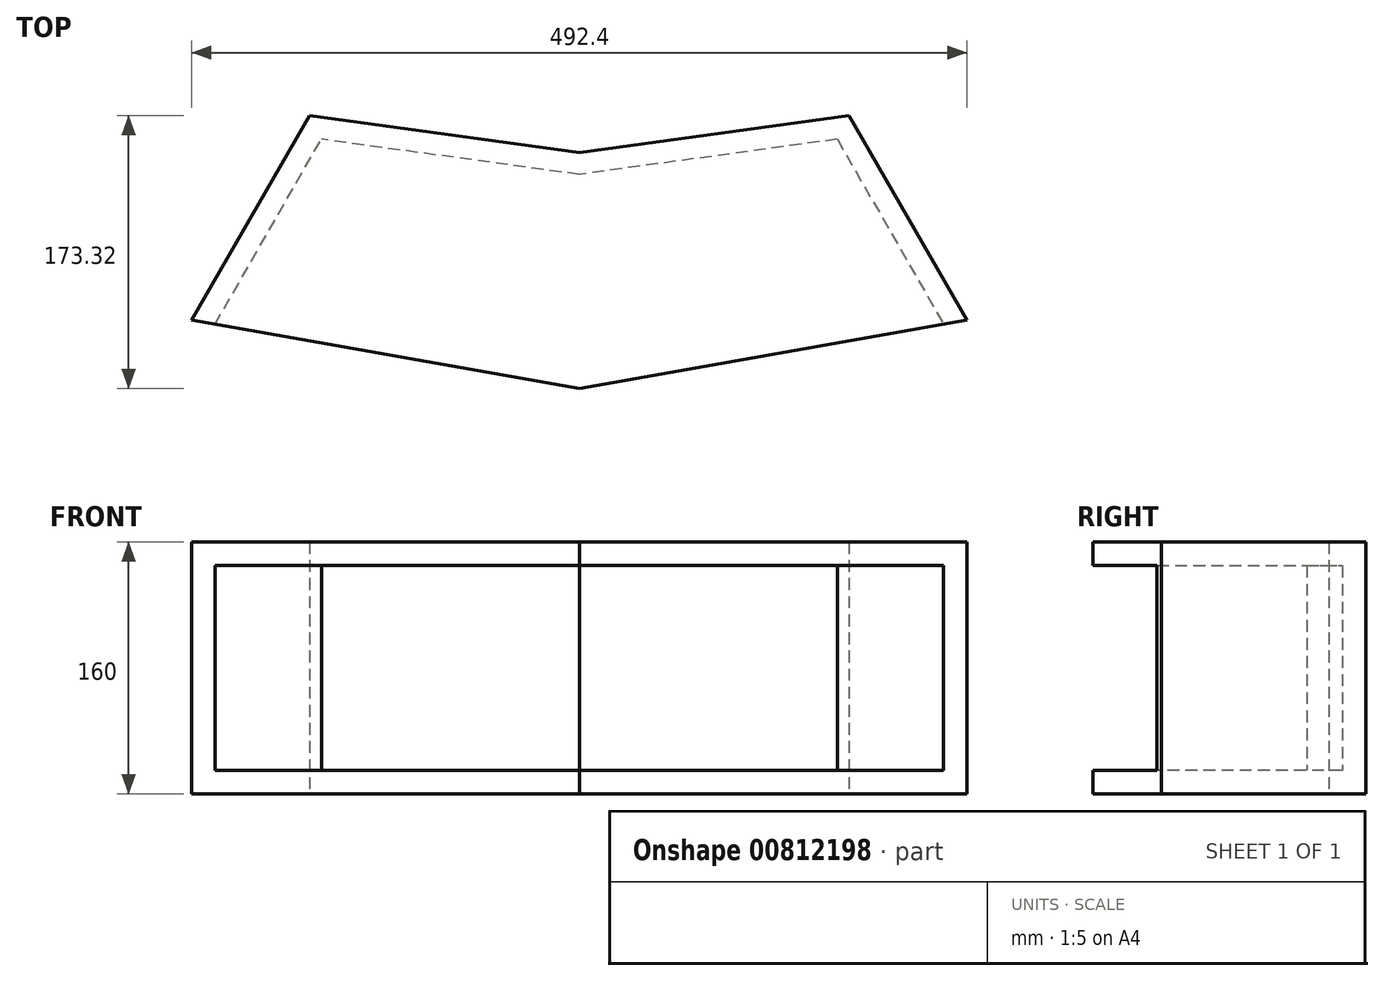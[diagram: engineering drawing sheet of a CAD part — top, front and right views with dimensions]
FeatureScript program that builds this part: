
annotation { "Feature Type Name" : "Feature", "Feature Type Description" : "" }
export const myFeature = defineFeature(function(context is Context, id is Id, definition is map)
    precondition{}
    {
        {
            var Q0;
            Q0=qCreatedBy(makeId("Top.planeOp"),FACE);
            var sketch = newSketch(context, id + "F0", { "sketchPlane" : qUnion([Q0])});
            skLineSegment(sketch, "E0", {"start": v(0, 0) * mm, "end": v(0, -150) * mm});
            skLineSegment(sketch, "E1", {"start": v(0, -150) * mm, "end": v(246.2, -106.59) * mm});
            skLineSegment(sketch, "E2", {"start": v(0, -150) * mm, "end": v(-246.2, -106.59) * mm});
            skLineSegment(sketch, "E3", {"start": v(-246.2, -106.59) * mm, "end": v(-171.2, 23.32) * mm});
            skLineSegment(sketch, "E4", {"start": v(246.2, -106.59) * mm, "end": v(171.2, 23.32) * mm});
            skLineSegment(sketch, "E5", {"start": v(171.2, 23.32) * mm, "end": v(0, 0) * mm});
            skLineSegment(sketch, "E6", {"start": v(0, 0) * mm, "end": v(-171.2, 23.32) * mm});
            skSolve(sketch);
        }
        {
            var Q0;
            Q0 = qSketchRegion(id + "F0", true);
            extrude(context, id + "F1", {"entities" : qUnion([Q0]), "depth" : 15 * mm, "offsetDistance" : 25.4 * mm});
        }
        {
            var Q0;
            Q0=makeQuery(id+"F1.opExtrude","CAP_FACE",FACE,{"disambiguationData":[OSD([sQuery(id+"F0.wireOp",EDGE,"E1"),sQuery(id+"F0.wireOp",EDGE,"E2"),sQuery(id+"F0.wireOp",EDGE,"E3"),sQuery(id+"F0.wireOp",EDGE,"E4"),sQuery(id+"F0.wireOp",EDGE,"E5"),sQuery(id+"F0.wireOp",EDGE,"E6")])],"isStart":false});
            var sketch = newSketch(context, id + "F2", { "sketchPlane" : qUnion([Q0])});
            skLineSegment(sketch, "E7", {"start": v(-246.2, -106.59) * mm, "end": v(-231.43, -109.2) * mm});
            skLineSegment(sketch, "E8", {"start": v(-231.43, -109.2) * mm, "end": v(-163.82, 8.3) * mm});
            skLineSegment(sketch, "E9", {"start": v(-156.34, 21.3) * mm, "end": v(-171.2, 23.32) * mm});
            skLineSegment(sketch, "E10", {"start": v(-171.2, 23.32) * mm, "end": v(-246.2, -106.59) * mm});
            skLineSegment(sketch, "E11", {"start": v(171.2, 23.32) * mm, "end": v(156.34, 21.3) * mm});
            skLineSegment(sketch, "E12", {"start": v(163.82, 8.3) * mm, "end": v(231.43, -109.2) * mm});
            skLineSegment(sketch, "E13", {"start": v(231.43, -109.2) * mm, "end": v(246.2, -106.59) * mm});
            skLineSegment(sketch, "E14", {"start": v(246.2, -106.59) * mm, "end": v(171.2, 23.32) * mm});
            skLineSegment(sketch, "E15", {"start": v(-156.34, 21.3) * mm, "end": v(0, 0) * mm});
            skLineSegment(sketch, "E16", {"start": v(0, 0) * mm, "end": v(156.34, 21.3) * mm});
            skLineSegment(sketch, "E17", {"start": v(163.82, 8.3) * mm, "end": v(0, -14.02) * mm});
            skLineSegment(sketch, "E18", {"start": v(0, -14.02) * mm, "end": v(-163.82, 8.3) * mm});
            skSolve(sketch);
        }
        {
            var Q0;
            Q0 = qSketchRegion(id + "F2", true);
            extrude(context, id + "F3", {"entities" : qUnion([Q0]), "operationType" : NewBodyOperationType.ADD, "depth" : 130 * mm, "offsetDistance" : 25.4 * mm});
        }
        {
            var Q0;
            Q0=makeQuery(id+"F3.opExtrude","CAP_FACE",FACE,{"disambiguationData":[OSD([sQuery(id+"F2.wireOp",EDGE,"E7"),sQuery(id+"F2.wireOp",EDGE,"E8"),sQuery(id+"F2.wireOp",EDGE,"E9"),sQuery(id+"F2.wireOp",EDGE,"E10"),sQuery(id+"F2.wireOp",EDGE,"E11"),sQuery(id+"F2.wireOp",EDGE,"E12"),sQuery(id+"F2.wireOp",EDGE,"E13"),sQuery(id+"F2.wireOp",EDGE,"E14"),sQuery(id+"F2.wireOp",EDGE,"E15"),sQuery(id+"F2.wireOp",EDGE,"E16"),sQuery(id+"F2.wireOp",EDGE,"E17"),sQuery(id+"F2.wireOp",EDGE,"E18")])],"isStart":false});
            var sketch = newSketch(context, id + "F4", { "sketchPlane" : qUnion([Q0])});
            skLineSegment(sketch, "E19", {"start": v(-246.2, -106.59) * mm, "end": v(-171.2, 23.32) * mm});
            skLineSegment(sketch, "E20", {"start": v(-171.2, 23.32) * mm, "end": v(0, 0) * mm});
            skLineSegment(sketch, "E21", {"start": v(0, 0) * mm, "end": v(171.2, 23.32) * mm});
            skLineSegment(sketch, "E22", {"start": v(171.2, 23.32) * mm, "end": v(246.2, -106.59) * mm});
            skLineSegment(sketch, "E23", {"start": v(246.2, -106.59) * mm, "end": v(0, -150) * mm});
            skLineSegment(sketch, "E24", {"start": v(0, -150) * mm, "end": v(-246.2, -106.59) * mm});
            skSolve(sketch);
        }
        {
            var Q0;
            Q0 = qSketchRegion(id + "F4", true);
            extrude(context, id + "F5", {"entities" : qUnion([Q0]), "operationType" : NewBodyOperationType.ADD, "depth" : 15 * mm, "offsetDistance" : 25.4 * mm});
        }
    });
